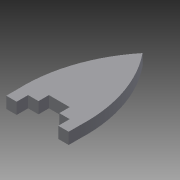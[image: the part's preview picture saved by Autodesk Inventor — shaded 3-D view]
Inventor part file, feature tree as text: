
AUTODESK INVENTOR PART (.ipt)
format: ipt  version: 2015 (Build 190159000, 159)  size: 82,432 bytes
history: native  units: mm
features: extrude x1, sketch x1
ambient origin geometry x8: Origin, YZ Plane, XZ Plane, XY Plane, X Axis, Y Axis, Z Axis, Center Point
bodies: Solid1 (feature_tree)
feature tree (2):
  extrude  "Extrusion1"  Depth=5.0mm
  sketch  "Sketch1"  dims[d1=5.5mm d2=5.0mm d3=5.5mm d4=0.0mm d5=10.0mm]
